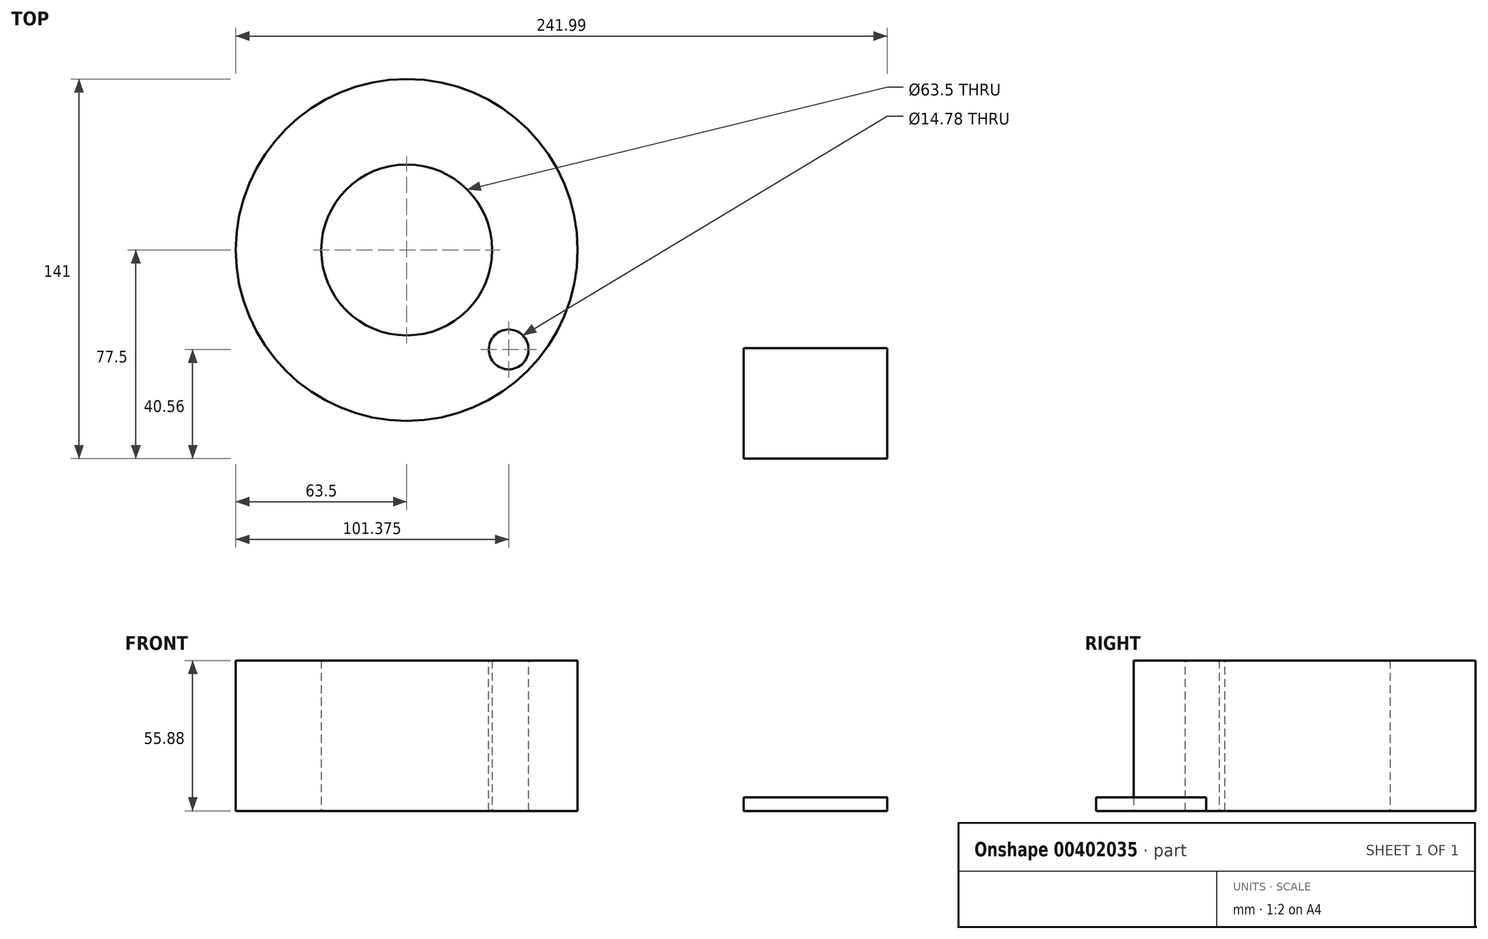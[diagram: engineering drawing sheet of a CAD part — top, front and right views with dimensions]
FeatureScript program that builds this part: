
annotation { "Feature Type Name" : "Feature", "Feature Type Description" : "" }
export const myFeature = defineFeature(function(context is Context, id is Id, definition is map)
    precondition{}
    {
        {
            var Q0;
            Q0=qCreatedBy(makeId("Top.planeOp"),FACE);
            var sketch = newSketch(context, id + "F0", { "sketchPlane" : qUnion([Q0])});
            skCircle(sketch, "E0", {"center": v(0, 0) * mm, "radius": 63.5 * mm});
            skCircle(sketch, "E1", {"center": v(0, 0) * mm, "radius": 31.75 * mm});
            skSolve(sketch);
        }
        {
            var Q0;
            Q0 = qSketchRegion(id + "F0", true);
            extrude(context, id + "F1", {"entities" : qUnion([Q0]), "depth" : 30.48 * mm});
        }
        {
            var Q0;
            Q0=makeQuery(id+"F1.opExtrude","CAP_FACE",FACE,{"disambiguationData":[OSD([sQuery(id+"F0.wireOp",EDGE,"E0"),sQuery(id+"F0.wireOp",EDGE,"E1")])],"isStart":false});
            var sketch = newSketch(context, id + "F2", { "sketchPlane" : qUnion([Q0])});
            skCircle(sketch, "E2", {"center": v(37.88, -36.94) * mm, "radius": 7.4 * mm});
            skSolve(sketch);
        }
        {
            var Q0;
            Q0=makeQuery(id+"F2.imprint","IMPRINT",FACE,{"disambiguationData":[TD([[makeQuery(id+"F2.imprint","IMPRINT",EDGE,{"derivedFrom":sQuery(id+"F2.wireOp",EDGE,"E2")}),1.0]])]});
            extrude(context, id + "F3", {"entities" : qUnion([Q0]), "operationType" : NewBodyOperationType.REMOVE, "oppositeDirection" : true, "depth" : 127 * mm});
        }
        {
            var Q0;
            Q0=makeQuery(id+"F1.opExtrude","CAP_FACE",FACE,{"disambiguationData":[OSD([sQuery(id+"F0.wireOp",EDGE,"E0"),sQuery(id+"F0.wireOp",EDGE,"E1")])],"isStart":false});
            extrude(context, id + "F4", {"entities" : qUnion([Q0]), "operationType" : NewBodyOperationType.ADD, "depth" : 25.4 * mm});
        }
        {
            var Q0;
            Q0=qCreatedBy(makeId("Top.planeOp"),FACE);
            var sketch = newSketch(context, id + "F5", { "sketchPlane" : qUnion([Q0])});
            skLineSegment(sketch, "E3.bottom", {"start": v(125.16, -77.5) * mm, "end": v(178.49, -77.5) * mm});
            skLineSegment(sketch, "E3.top", {"start": v(125.16, -36.48) * mm, "end": v(178.49, -36.48) * mm});
            skLineSegment(sketch, "E3.left", {"start": v(125.16, -77.5) * mm, "end": v(125.16, -36.48) * mm});
            skLineSegment(sketch, "E3.right", {"start": v(178.49, -77.5) * mm, "end": v(178.49, -36.48) * mm});
            skSolve(sketch);
        }
        {
            var Q0;
            Q0 = qSketchRegion(id + "F5", true);
            extrude(context, id + "F6", {"entities" : qUnion([Q0]), "depth" : 5.08 * mm});
        }
    });
